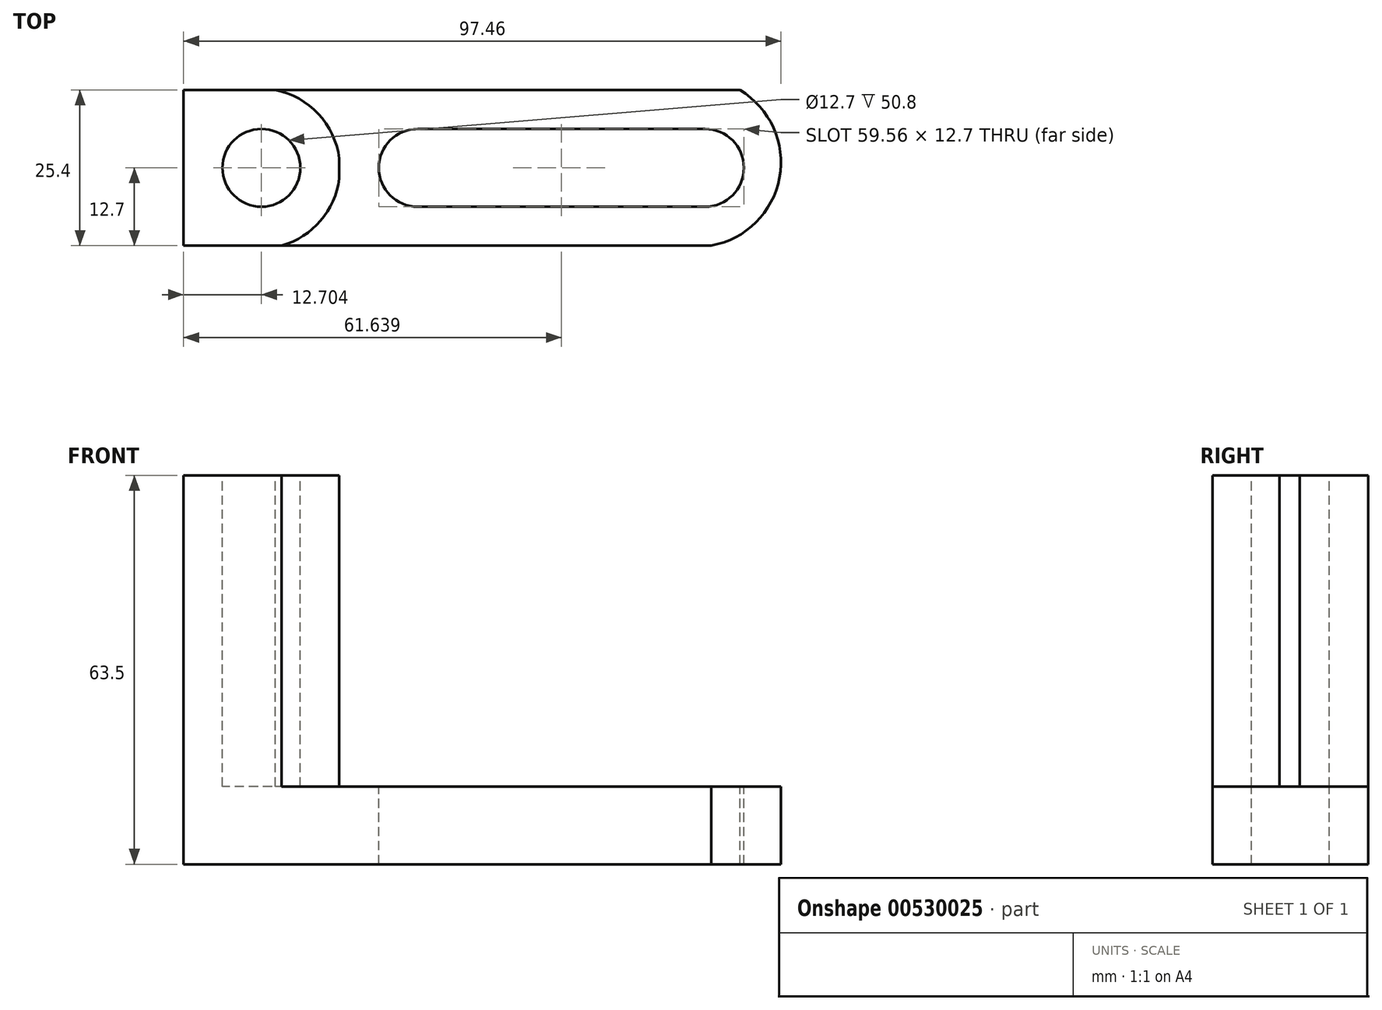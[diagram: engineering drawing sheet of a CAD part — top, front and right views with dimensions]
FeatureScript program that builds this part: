
annotation { "Feature Type Name" : "Feature", "Feature Type Description" : "" }
export const myFeature = defineFeature(function(context is Context, id is Id, definition is map)
    precondition{}
    {
        {
            var Q0;
            Q0=qCreatedBy(makeId("Front.planeOp"),FACE);
            var sketch = newSketch(context, id + "F0", { "sketchPlane" : qUnion([Q0])});
            skLineSegment(sketch, "E0", {"start": v(-76.55, 63.5) * mm, "end": v(-76.55, 0) * mm});
            skLineSegment(sketch, "E1", {"start": v(-76.55, 0) * mm, "end": v(21.22, 0) * mm});
            skLineSegment(sketch, "E2", {"start": v(21.22, 0) * mm, "end": v(21.22, 12.7) * mm});
            skLineSegment(sketch, "E3", {"start": v(21.22, 12.7) * mm, "end": v(-51.15, 12.7) * mm});
            skLineSegment(sketch, "E4", {"start": v(-51.15, 12.7) * mm, "end": v(-51.15, 63.5) * mm});
            skLineSegment(sketch, "E5", {"start": v(-76.55, 63.5) * mm, "end": v(-51.15, 63.5) * mm});
            skSolve(sketch);
        }
        {
            var Q0;
            Q0=makeQuery(id+"F0.imprint","IMPRINT",FACE,{"disambiguationData":[TD([[makeQuery(id+"F0.imprint","IMPRINT",EDGE,{"derivedFrom":sQuery(id+"F0.wireOp",EDGE,"E0")}),1.0]])]});
            extrude(context, id + "F1", {"entities" : qUnion([Q0]), "depth" : 25.4 * mm, "offsetDistance" : 25.4 * mm});
        }
        {
            var Q0;
            Q0=makeQuery(id+"F1.opExtrude","SWEPT_FACE",FACE,{"disambiguationData":[OSD([sQuery(id+"F0.wireOp",EDGE,"E5")])]});
            var sketch = newSketch(context, id + "F2", { "sketchPlane" : qUnion([Q0])});
            skArc(sketch, "E6", {"start": v(-60.54, -25.4) * mm, "mid": v(-51.05, -12.3) * mm, "end": v(-61.57, 0) * mm});
            skCircle(sketch, "E7", {"center": v(-63.85, -12.7) * mm, "radius": 6.35 * mm});
            skSolve(sketch);
        }
        {
            var Q0;
            {var subQ0=sQuery(id+"F2.wireOp",EDGE,"E6");var subQ1=sQuery(id+"F0.wireOp",EDGE,"E5");var subQ2=makeQuery(id+"F1.opExtrude","CAP_EDGE",EDGE,{"disambiguationData":[OSD([subQ1])],"isStart":false});var subQ3=makeQuery(id+"F2.imprint","INTERSECT",VERTEX,{"derivedFrom":[subQ2,subQ0]});Q0=makeQuery(id+"F2.imprint","IMPRINT",FACE,{"disambiguationData":[TD([[makeQuery(id+"F2.imprint","IMPRINT",EDGE,{"disambiguationData":[TD([[subQ3,-1.0]])],"derivedFrom":subQ0}),-1.0]])]});}
            var Q1;
            {var subQ0=sQuery(id+"F2.wireOp",EDGE,"E6");var subQ1=sQuery(id+"F0.wireOp",EDGE,"E5");var subQ2=makeQuery(id+"F1.opExtrude","CAP_EDGE",EDGE,{"disambiguationData":[OSD([subQ1])],"isStart":true});var subQ3=makeQuery(id+"F2.imprint","INTERSECT",VERTEX,{"derivedFrom":[subQ2,subQ0]});Q1=makeQuery(id+"F2.imprint","IMPRINT",FACE,{"disambiguationData":[TD([[makeQuery(id+"F2.imprint","IMPRINT",EDGE,{"disambiguationData":[TD([[subQ3,1.0]])],"derivedFrom":subQ0}),-1.0]])]});}
            extrude(context, id + "F3", {"entities" : qUnion([Q0, Q1]), "operationType" : NewBodyOperationType.REMOVE, "oppositeDirection" : true, "depth" : 50.8 * mm, "offsetDistance" : 25.4 * mm});
        }
        {
            var Q0;
            Q0 = qSketchRegion(id + "F2", true);
            extrude(context, id + "F4", {"entities" : qUnion([Q0]), "operationType" : NewBodyOperationType.REMOVE, "oppositeDirection" : true, "depth" : 50.8 * mm, "offsetDistance" : 25.4 * mm});
        }
        {
            var Q0;
            {var subQ0=sQuery(id+"F0.wireOp",EDGE,"E5");var subQ1=makeQuery(id+"F1.opExtrude","CAP_EDGE",EDGE,{"disambiguationData":[OSD([subQ0])],"isStart":true});var subQ2=sQuery(id+"F0.wireOp",EDGE,"E4");var subQ3=makeQuery(id+"F1.opExtrude","SWEPT_EDGE",EDGE,{"disambiguationData":[OSD([subQ2,subQ0])]});var subQ4=makeQuery(id+"F2.imprint","INTERSECT",VERTEX,{"derivedFrom":[subQ3,subQ1]});var subQ5=sQuery(id+"F2.wireOp",EDGE,"E6");var subQ6=makeQuery(id+"F2.imprint","INTERSECT",VERTEX,{"derivedFrom":[subQ1,subQ5]});var subQ8=makeQuery(id+"F1.opExtrude","CAP_EDGE",EDGE,{"disambiguationData":[OSD([subQ0])],"isStart":false});var subQ9=makeQuery(id+"F2.imprint","INTERSECT",VERTEX,{"derivedFrom":[subQ3,subQ8]});var subQ10=makeQuery(id+"F2.imprint","INTERSECT",VERTEX,{"derivedFrom":[subQ8,subQ5]});Q0=makeQuery(id+"F3.boolean.opBoolean","MERGE",FACE,{"derivedFrom":[makeQuery(id+"F1.opExtrude","SWEPT_FACE",FACE,{"disambiguationData":[OSD([sQuery(id+"F0.wireOp",EDGE,"E3")])]}),makeQuery(id+"F3.opExtrude","CAP_FACE",FACE,{"disambiguationData":[OSD([subQ2,subQ0,subQ5]),TDD([makeQuery(id+"F2.imprint","IMPRINT",EDGE,{"disambiguationData":[TD([[subQ10,-1.0]])],"derivedFrom":subQ5}),makeQuery(id+"F2.imprint","IMPRINT",EDGE,{"disambiguationData":[TD([[subQ9,-1.0]])],"derivedFrom":subQ3}),makeQuery(id+"F2.imprint","IMPRINT",EDGE,{"disambiguationData":[TD([[subQ10,-1.0]])],"derivedFrom":subQ8})])],"isStart":false}),makeQuery(id+"F3.opExtrude","CAP_FACE",FACE,{"disambiguationData":[OSD([subQ2,subQ0,subQ5]),TDD([makeQuery(id+"F2.imprint","IMPRINT",EDGE,{"disambiguationData":[TD([[subQ6,1.0]])],"derivedFrom":subQ5}),makeQuery(id+"F2.imprint","IMPRINT",EDGE,{"disambiguationData":[TD([[subQ4,1.0]])],"derivedFrom":subQ3}),makeQuery(id+"F2.imprint","IMPRINT",EDGE,{"disambiguationData":[TD([[subQ6,-1.0]])],"derivedFrom":subQ1})])],"isStart":false})]});}
            var sketch = newSketch(context, id + "F5", { "sketchPlane" : qUnion([Q0])});
            skCircle(sketch, "E8", {"center": v(-38.34, -12.7) * mm, "radius": 6.35 * mm});
            skCircle(sketch, "E9", {"center": v(8.52, -12.7) * mm, "radius": 6.35 * mm});
            skLineSegment(sketch, "E10", {"start": v(-38.34, -19.05) * mm, "end": v(8.52, -19.05) * mm});
            skLineSegment(sketch, "E11", {"start": v(-38.34, -6.35) * mm, "end": v(8.52, -6.35) * mm});
            skSolve(sketch);
        }
        {
            var Q0;
            {var subQ0=sQuery(id+"F5.wireOp",EDGE,"E10");Q0=makeQuery(id+"F5.imprint","IMPRINT",FACE,{"disambiguationData":[TD([[makeQuery(id+"F5.imprint","IMPRINT",EDGE,{"derivedFrom":subQ0}),1.0]])]});}
            var Q1;
            {var subQ0=sQuery(id+"F5.wireOp",EDGE,"E9");var subQ1=makeQuery(id+"F5.imprint","INTERSECT",VERTEX,{"derivedFrom":[subQ0,sQuery(id+"F5.wireOp",EDGE,"E10")]});Q1=makeQuery(id+"F5.imprint","IMPRINT",FACE,{"disambiguationData":[TD([[makeQuery(id+"F5.imprint","IMPRINT",EDGE,{"disambiguationData":[TD([[subQ1,1.0]])],"derivedFrom":subQ0}),1.0]])]});}
            var Q2;
            {var subQ0=sQuery(id+"F5.wireOp",EDGE,"E8");var subQ1=makeQuery(id+"F5.imprint","INTERSECT",VERTEX,{"derivedFrom":[subQ0,sQuery(id+"F5.wireOp",EDGE,"E10")]});Q2=makeQuery(id+"F5.imprint","IMPRINT",FACE,{"disambiguationData":[TD([[makeQuery(id+"F5.imprint","IMPRINT",EDGE,{"disambiguationData":[TD([[subQ1,1.0]])],"derivedFrom":subQ0}),1.0]])]});}
            extrude(context, id + "F6", {"entities" : qUnion([Q0, Q1, Q2]), "operationType" : NewBodyOperationType.REMOVE, "endBound" : BoundingType.THROUGH_ALL, "oppositeDirection" : true, "depth" : 127 * mm, "offsetDistance" : 25.4 * mm});
        }
        {
            var Q0;
            {var subQ0=sQuery(id+"F0.wireOp",EDGE,"E5");var subQ1=makeQuery(id+"F1.opExtrude","CAP_EDGE",EDGE,{"disambiguationData":[OSD([subQ0])],"isStart":true});var subQ2=sQuery(id+"F0.wireOp",EDGE,"E4");var subQ3=makeQuery(id+"F1.opExtrude","SWEPT_EDGE",EDGE,{"disambiguationData":[OSD([subQ2,subQ0])]});var subQ4=makeQuery(id+"F2.imprint","INTERSECT",VERTEX,{"derivedFrom":[subQ3,subQ1]});var subQ5=sQuery(id+"F2.wireOp",EDGE,"E6");var subQ6=makeQuery(id+"F2.imprint","INTERSECT",VERTEX,{"derivedFrom":[subQ1,subQ5]});var subQ8=makeQuery(id+"F1.opExtrude","CAP_EDGE",EDGE,{"disambiguationData":[OSD([subQ0])],"isStart":false});var subQ9=makeQuery(id+"F2.imprint","INTERSECT",VERTEX,{"derivedFrom":[subQ3,subQ8]});var subQ10=makeQuery(id+"F2.imprint","INTERSECT",VERTEX,{"derivedFrom":[subQ8,subQ5]});Q0=makeQuery(id+"F3.boolean.opBoolean","MERGE",FACE,{"derivedFrom":[makeQuery(id+"F1.opExtrude","SWEPT_FACE",FACE,{"disambiguationData":[OSD([sQuery(id+"F0.wireOp",EDGE,"E3")])]}),makeQuery(id+"F3.opExtrude","CAP_FACE",FACE,{"disambiguationData":[OSD([subQ2,subQ0,subQ5]),TDD([makeQuery(id+"F2.imprint","IMPRINT",EDGE,{"disambiguationData":[TD([[subQ10,-1.0]])],"derivedFrom":subQ5}),makeQuery(id+"F2.imprint","IMPRINT",EDGE,{"disambiguationData":[TD([[subQ9,-1.0]])],"derivedFrom":subQ3}),makeQuery(id+"F2.imprint","IMPRINT",EDGE,{"disambiguationData":[TD([[subQ10,-1.0]])],"derivedFrom":subQ8})])],"isStart":false}),makeQuery(id+"F3.opExtrude","CAP_FACE",FACE,{"disambiguationData":[OSD([subQ2,subQ0,subQ5]),TDD([makeQuery(id+"F2.imprint","IMPRINT",EDGE,{"disambiguationData":[TD([[subQ6,1.0]])],"derivedFrom":subQ5}),makeQuery(id+"F2.imprint","IMPRINT",EDGE,{"disambiguationData":[TD([[subQ4,1.0]])],"derivedFrom":subQ3}),makeQuery(id+"F2.imprint","IMPRINT",EDGE,{"disambiguationData":[TD([[subQ6,-1.0]])],"derivedFrom":subQ1})])],"isStart":false})]});}
            var sketch = newSketch(context, id + "F7", { "sketchPlane" : qUnion([Q0])});
            skArc(sketch, "E12", {"start": v(4.71, -25.4) * mm, "mid": v(20.68, -9.3) * mm, "end": v(0, 0) * mm});
            skSolve(sketch);
        }
        {
            var Q0;
            {var subQ5=sQuery(id+"F0.wireOp",EDGE,"E3");var subQ11=makeQuery(id+"F1.opExtrude","SWEPT_EDGE",EDGE,{"disambiguationData":[OSD([sQuery(id+"F0.wireOp",EDGE,"E2"),subQ5])]});Q0=makeQuery(id+"F7.imprint","IMPRINT",FACE,{"disambiguationData":[TD([[makeQuery(id+"F7.imprint","IMPRINT",EDGE,{"derivedFrom":subQ11}),1.0]])]});}
            extrude(context, id + "F8", {"entities" : qUnion([Q0]), "operationType" : NewBodyOperationType.REMOVE, "endBound" : BoundingType.THROUGH_ALL, "oppositeDirection" : true, "depth" : 25.4 * mm, "offsetDistance" : 25.4 * mm});
        }
    });
